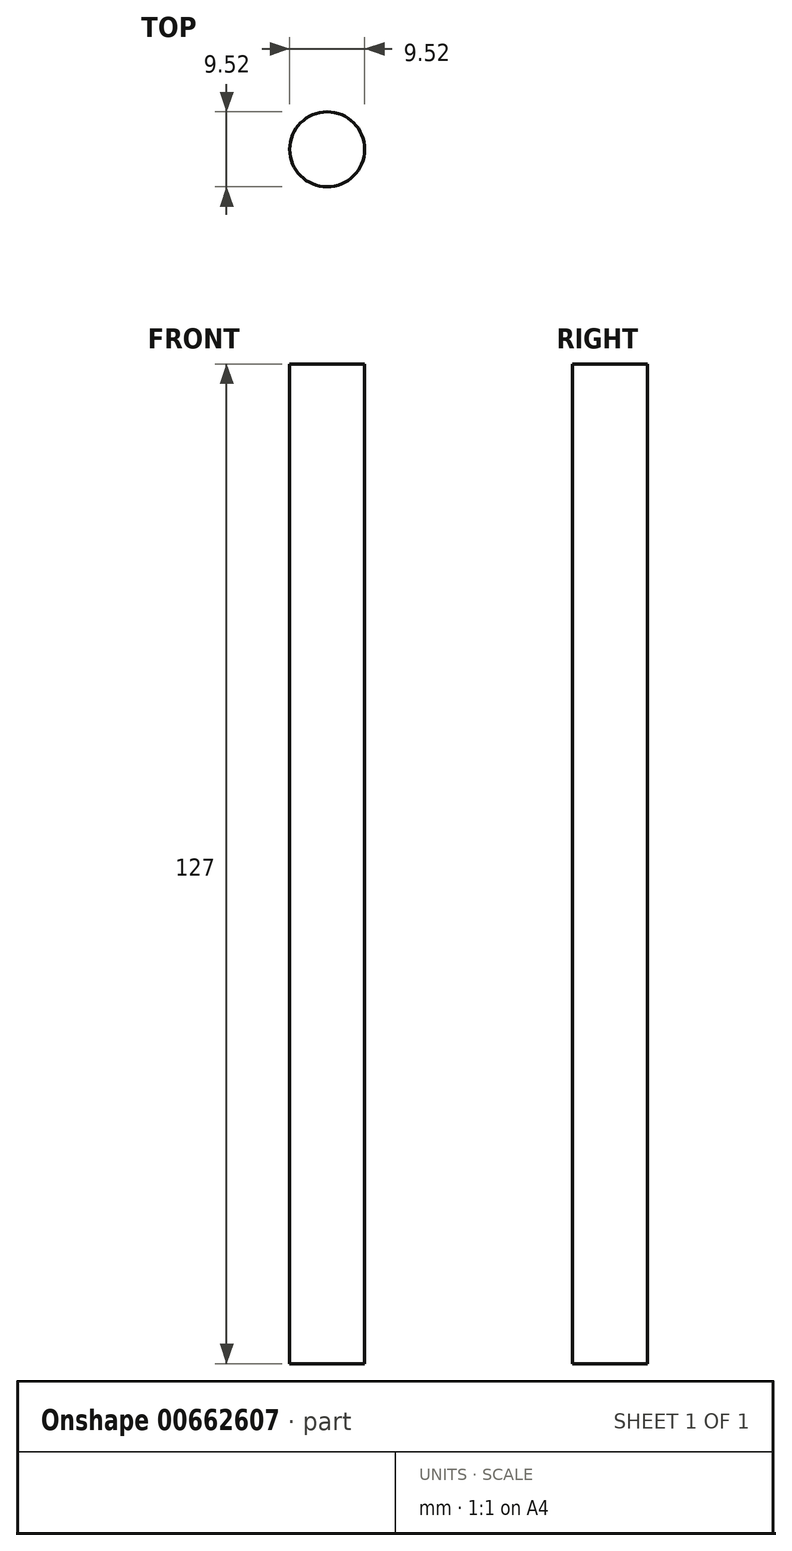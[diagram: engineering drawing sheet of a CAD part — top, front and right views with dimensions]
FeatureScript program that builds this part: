
annotation { "Feature Type Name" : "Feature", "Feature Type Description" : "" }
export const myFeature = defineFeature(function(context is Context, id is Id, definition is map)
    precondition{}
    {
        {
            var Q0;
            Q0=qCreatedBy(makeId("Top.planeOp"),FACE);
            var sketch = newSketch(context, id + "F0", { "sketchPlane" : qUnion([Q0])});
            skCircle(sketch, "E0", {"center": v(0, 0) * mm, "radius": 4.76 * mm});
            skSolve(sketch);
        }
        {
            var Q0;
            Q0=makeQuery(id+"F0.imprint","IMPRINT",FACE,{"disambiguationData":[TD([[makeQuery(id+"F0.imprint","IMPRINT",EDGE,{"derivedFrom":sQuery(id+"F0.wireOp",EDGE,"E0")}),1.0]])]});
            extrude(context, id + "F1", {"entities" : qUnion([Q0]), "depth" : 127 * mm, "offsetDistance" : 25.4 * mm});
        }
    });
